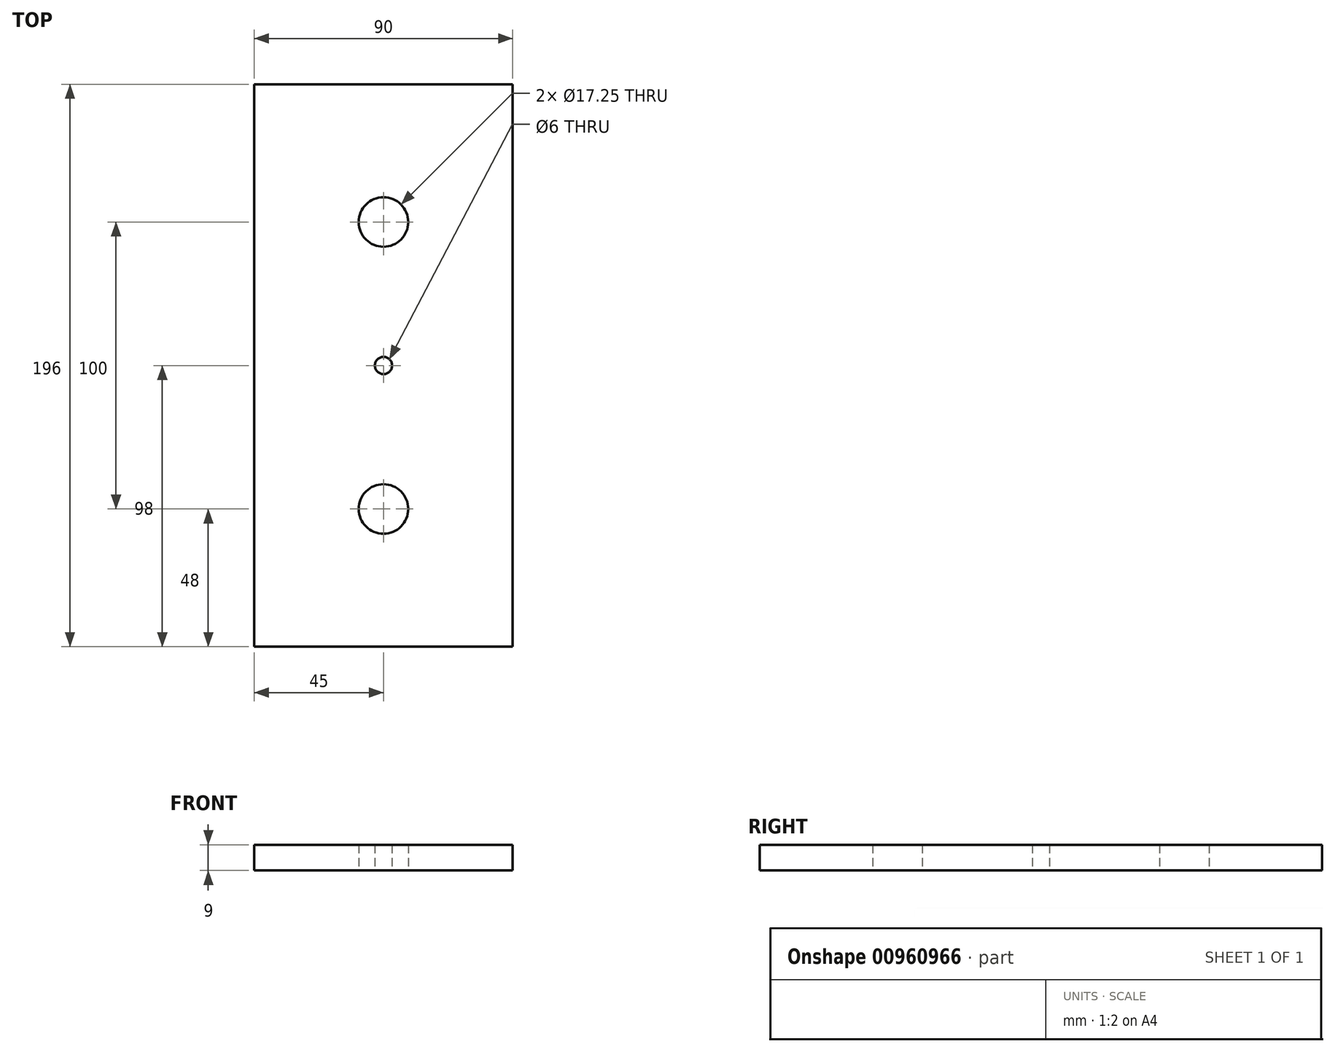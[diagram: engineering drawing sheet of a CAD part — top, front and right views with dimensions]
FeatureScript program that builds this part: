
annotation { "Feature Type Name" : "Feature", "Feature Type Description" : "" }
export const myFeature = defineFeature(function(context is Context, id is Id, definition is map)
    precondition{}
    {
        {
            var Q0;
            Q0=qCreatedBy(makeId("Top.planeOp"),FACE);
            var sketch = newSketch(context, id + "F0", { "sketchPlane" : qUnion([Q0])});
            skLineSegment(sketch, "E0.bottom", {"start": v(-45, 98) * mm, "end": v(45, 98) * mm});
            skLineSegment(sketch, "E0.top", {"start": v(-45, -98) * mm, "end": v(45, -98) * mm});
            skLineSegment(sketch, "E0.left", {"start": v(-45, 98) * mm, "end": v(-45, -98) * mm});
            skLineSegment(sketch, "E0.right", {"start": v(45, 98) * mm, "end": v(45, -98) * mm});
            skLineSegment(sketch, "E1", {"start": v(0, -98) * mm, "end": v(0, 98) * mm, "construction": true});
            skCircle(sketch, "E2", {"center": v(0, 0) * mm, "radius": 3 * mm});
            skCircle(sketch, "E3", {"center": v(0, 50) * mm, "radius": 8.62 * mm});
            skCircle(sketch, "E4.MirrorC", {"center": v(0, -50) * mm, "radius": 8.62 * mm});
            skSolve(sketch);
        }
        {
            var Q0;
            Q0=makeQuery(id+"F0.imprint","IMPRINT",FACE,{"disambiguationData":[TD([[makeQuery(id+"F0.imprint","IMPRINT",EDGE,{"derivedFrom":sQuery(id+"F0.wireOp",EDGE,"E0.bottom")}),-1.0]])]});
            extrude(context, id + "F1", {"entities" : qUnion([Q0]), "depth" : 9 * mm, "offsetDistance" : 25 * mm});
        }
    });
